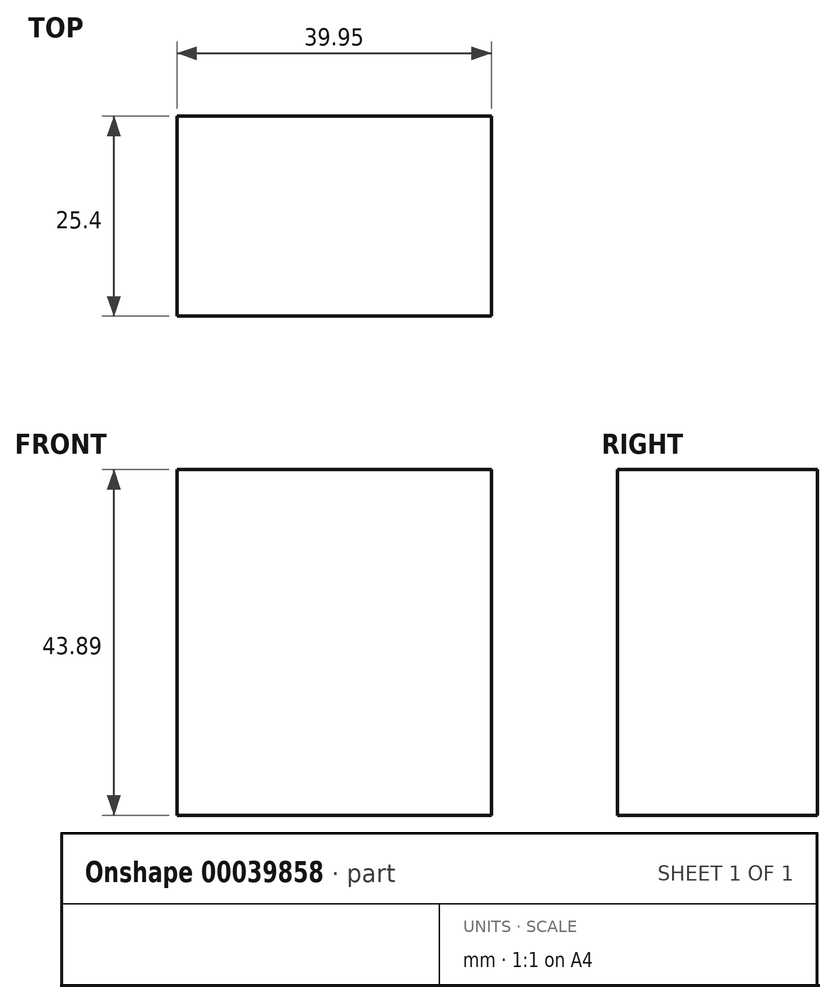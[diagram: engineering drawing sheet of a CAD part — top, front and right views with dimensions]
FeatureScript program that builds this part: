
annotation { "Feature Type Name" : "Feature", "Feature Type Description" : "" }
export const myFeature = defineFeature(function(context is Context, id is Id, definition is map)
    precondition{}
    {
        {
            var Q0;
            Q0=qCreatedBy(makeId("Front.planeOp"),FACE);
            var sketch = newSketch(context, id + "F0", { "sketchPlane" : qUnion([Q0])});
            skLineSegment(sketch, "E0.bottom", {"start": v(0, 0) * mm, "end": v(39.95, 0) * mm});
            skLineSegment(sketch, "E0.top", {"start": v(0, 43.9) * mm, "end": v(39.95, 43.9) * mm});
            skLineSegment(sketch, "E0.left", {"start": v(0, 0) * mm, "end": v(0, 43.9) * mm});
            skLineSegment(sketch, "E0.right", {"start": v(39.95, 0) * mm, "end": v(39.95, 43.9) * mm});
            skSolve(sketch);
        }
        {
            var Q0;
            Q0 = qSketchRegion(id + "F0", true);
            extrude(context, id + "F1", {"entities" : qUnion([Q0]), "depth" : 25.4 * mm});
        }
    });
